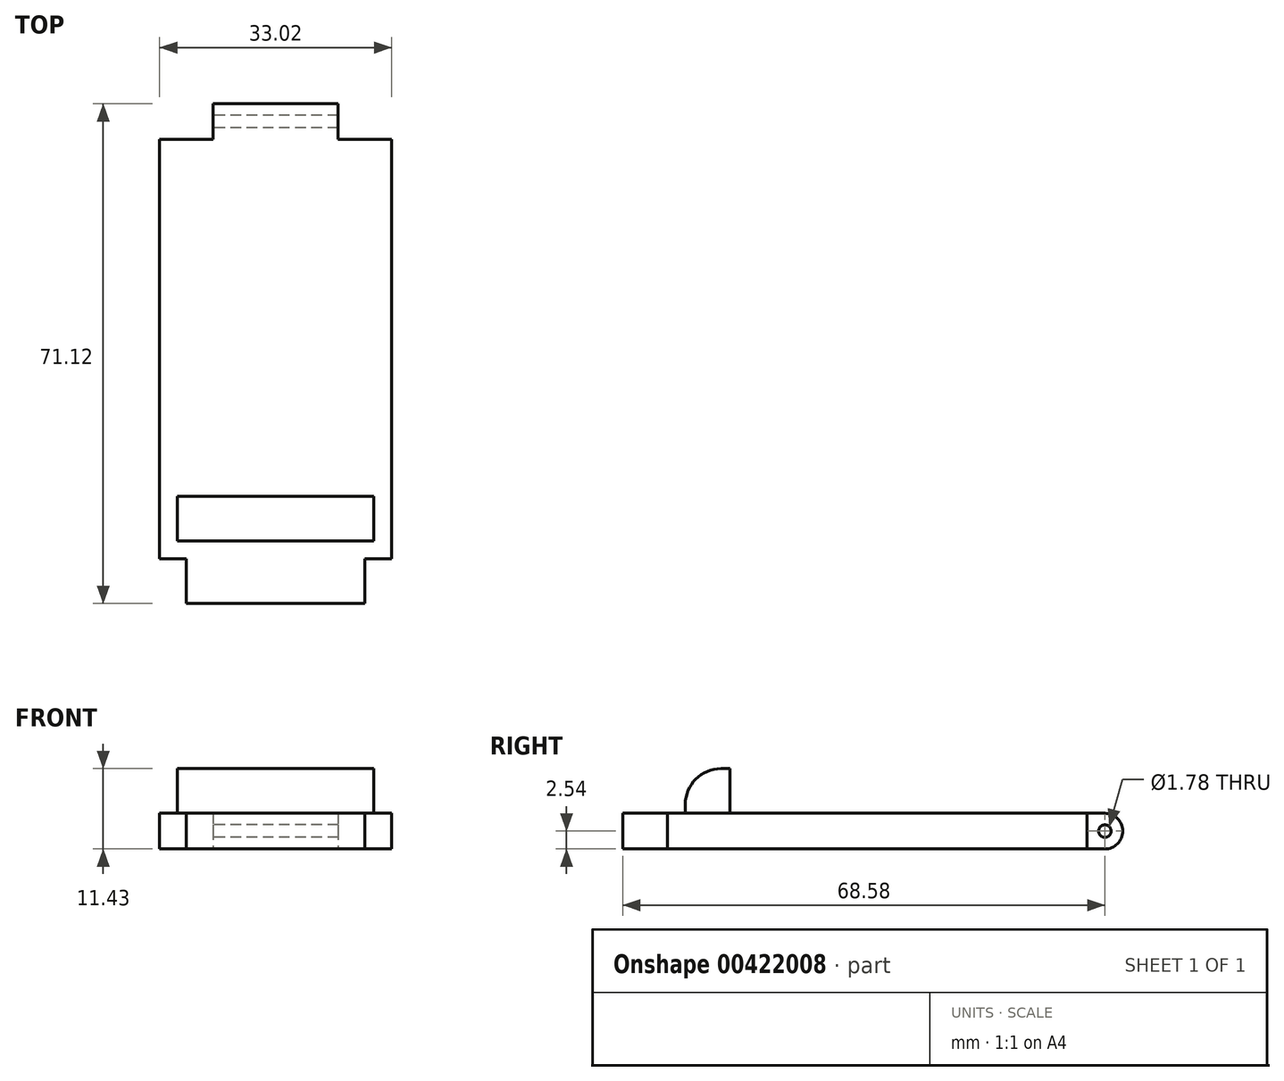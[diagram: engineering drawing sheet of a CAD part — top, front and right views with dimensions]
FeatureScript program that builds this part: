
annotation { "Feature Type Name" : "Feature", "Feature Type Description" : "" }
export const myFeature = defineFeature(function(context is Context, id is Id, definition is map)
    precondition{}
    {
        {
            var Q0;
            Q0=qCreatedBy(makeId("Top.planeOp"),FACE);
            var sketch = newSketch(context, id + "F0", { "sketchPlane" : qUnion([Q0])});
            skLineSegment(sketch, "E0.bottom", {"start": v(0, 0) * mm, "end": v(33.02, 0) * mm});
            skLineSegment(sketch, "E0.top", {"start": v(0, 59.69) * mm, "end": v(33.02, 59.69) * mm});
            skLineSegment(sketch, "E0.left", {"start": v(0, 0) * mm, "end": v(0, 59.69) * mm});
            skLineSegment(sketch, "E0.right", {"start": v(33.02, 0) * mm, "end": v(33.02, 59.69) * mm});
            skSolve(sketch);
        }
        {
            var Q0;
            Q0=makeQuery(id+"F0.imprint","IMPRINT",FACE,{"disambiguationData":[TD([[makeQuery(id+"F0.imprint","IMPRINT",EDGE,{"derivedFrom":sQuery(id+"F0.wireOp",EDGE,"E0.bottom")}),1.0]])]});
            extrude(context, id + "F1", {"entities" : qUnion([Q0]), "depth" : 5.08 * mm});
        }
        {
            var Q0;
            Q0=makeQuery(id+"F1.opExtrude","SWEPT_FACE",FACE,{"disambiguationData":[OSD([sQuery(id+"F0.wireOp",EDGE,"E0.top")])]});
            var sketch = newSketch(context, id + "F2", { "sketchPlane" : qUnion([Q0])});
            skLineSegment(sketch, "E1.bottom", {"start": v(-7.62, 5.08) * mm, "end": v(-25.4, 5.08) * mm});
            skLineSegment(sketch, "E1.top", {"start": v(-7.62, 0) * mm, "end": v(-25.4, 0) * mm});
            skLineSegment(sketch, "E1.left", {"start": v(-7.62, 5.08) * mm, "end": v(-7.62, 0) * mm});
            skLineSegment(sketch, "E1.right", {"start": v(-25.4, 5.08) * mm, "end": v(-25.4, 0) * mm});
            skSolve(sketch);
        }
        {
            var Q0;
            Q0=makeQuery(id+"F2.imprint","IMPRINT",FACE,{"disambiguationData":[TD([[makeQuery(id+"F2.imprint","IMPRINT",EDGE,{"derivedFrom":sQuery(id+"F2.wireOp",EDGE,"E1.bottom")}),1.0]])]});
            extrude(context, id + "F3", {"entities" : qUnion([Q0]), "operationType" : NewBodyOperationType.ADD, "depth" : 5.08 * mm});
        }
        {
            var Q0;
            Q0=makeQuery(id+"F3.opExtrude","SWEPT_FACE",FACE,{"disambiguationData":[OSD([sQuery(id+"F2.wireOp",EDGE,"E1.left")])]});
            var sketch = newSketch(context, id + "F4", { "sketchPlane" : qUnion([Q0])});
            skLineSegment(sketch, "E2", {"start": v(-62.23, 5.08) * mm, "end": v(-62.23, 0) * mm, "construction": true});
            skCircle(sketch, "E3", {"center": v(-62.23, 2.54) * mm, "radius": 0.89 * mm});
            skSolve(sketch);
        }
        {
            var Q0;
            Q0=makeQuery(id+"F4.imprint","IMPRINT",FACE,{"disambiguationData":[TD([[makeQuery(id+"F4.imprint","IMPRINT",EDGE,{"derivedFrom":sQuery(id+"F4.wireOp",EDGE,"E3")}),1.0]])]});
            extrude(context, id + "F5", {"entities" : qUnion([Q0]), "operationType" : NewBodyOperationType.REMOVE, "oppositeDirection" : true, "depth" : 17.78 * mm});
        }
        {
            var Q0;
            Q0=makeQuery(id+"F3.opExtrude","CAP_EDGE",EDGE,{"disambiguationData":[OSD([sQuery(id+"F2.wireOp",EDGE,"E1.top")])],"isStart":false});
            var Q1;
            Q1=makeQuery(id+"F3.opExtrude","CAP_EDGE",EDGE,{"disambiguationData":[OSD([sQuery(id+"F2.wireOp",EDGE,"E1.bottom")])],"isStart":false});
            fillet(context, id + "F6", {"entities" : qUnion([Q0, Q1]), "radius" : 2.54 * mm, "tangentPropagation" : true, "allowEdgeOverflow" : false});
        }
        {
            var Q0;
            Q0=makeQuery(id+"F3.boolean.opBoolean","MERGE",FACE,{"derivedFrom":[makeQuery(id+"F1.opExtrude","CAP_FACE",FACE,{"disambiguationData":[OSD([sQuery(id+"F0.wireOp",EDGE,"E0.bottom"),sQuery(id+"F0.wireOp",EDGE,"E0.top"),sQuery(id+"F0.wireOp",EDGE,"E0.left"),sQuery(id+"F0.wireOp",EDGE,"E0.right")])],"isStart":false}),makeQuery(id+"F3.opExtrude","SWEPT_FACE",FACE,{"disambiguationData":[OSD([sQuery(id+"F2.wireOp",EDGE,"E1.bottom")])]})]});
            var sketch = newSketch(context, id + "F7", { "sketchPlane" : qUnion([Q0])});
            skLineSegment(sketch, "E4.bottom", {"start": v(2.54, 2.54) * mm, "end": v(30.48, 2.54) * mm});
            skLineSegment(sketch, "E4.top", {"start": v(2.54, 8.89) * mm, "end": v(30.48, 8.9) * mm});
            skLineSegment(sketch, "E4.left", {"start": v(2.54, 2.54) * mm, "end": v(2.54, 8.89) * mm});
            skLineSegment(sketch, "E4.right", {"start": v(30.48, 2.54) * mm, "end": v(30.48, 8.9) * mm});
            skSolve(sketch);
        }
        {
            var Q0;
            Q0=makeQuery(id+"F7.imprint","IMPRINT",FACE,{"disambiguationData":[TD([[makeQuery(id+"F7.imprint","IMPRINT",EDGE,{"derivedFrom":sQuery(id+"F7.wireOp",EDGE,"E4.bottom")}),1.0]])]});
            extrude(context, id + "F8", {"entities" : qUnion([Q0]), "operationType" : NewBodyOperationType.ADD, "depth" : 6.35 * mm});
        }
        {
            var Q0;
            Q0=makeQuery(id+"F8.opExtrude","CAP_EDGE",EDGE,{"disambiguationData":[OSD([sQuery(id+"F7.wireOp",EDGE,"E4.bottom")])],"isStart":false});
            fillet(context, id + "F9", {"entities" : qUnion([Q0]), "radius" : 5.08 * mm, "tangentPropagation" : true, "allowEdgeOverflow" : false});
        }
        {
            var Q0;
            Q0=makeQuery(id+"F1.opExtrude","SWEPT_FACE",FACE,{"disambiguationData":[OSD([sQuery(id+"F0.wireOp",EDGE,"E0.bottom")])]});
            var sketch = newSketch(context, id + "F10", { "sketchPlane" : qUnion([Q0])});
            skLineSegment(sketch, "E5.bottom", {"start": v(3.81, 0) * mm, "end": v(29.21, 0) * mm});
            skLineSegment(sketch, "E5.top", {"start": v(3.81, 5.08) * mm, "end": v(29.21, 5.08) * mm});
            skLineSegment(sketch, "E5.left", {"start": v(3.81, 0) * mm, "end": v(3.81, 5.08) * mm});
            skLineSegment(sketch, "E5.right", {"start": v(29.21, 0) * mm, "end": v(29.21, 5.08) * mm});
            skLineSegment(sketch, "E6", {"start": v(3.81, 2.54) * mm, "end": v(0, 2.54) * mm, "construction": true});
            skLineSegment(sketch, "E7", {"start": v(29.21, 2.54) * mm, "end": v(33.02, 2.54) * mm, "construction": true});
            skSolve(sketch);
        }
        {
            var Q0;
            Q0=makeQuery(id+"F10.imprint","IMPRINT",FACE,{"disambiguationData":[TD([[makeQuery(id+"F10.imprint","IMPRINT",EDGE,{"derivedFrom":sQuery(id+"F10.wireOp",EDGE,"E5.bottom")}),1.0]])]});
            extrude(context, id + "F11", {"entities" : qUnion([Q0]), "operationType" : NewBodyOperationType.ADD, "depth" : 6.35 * mm});
        }
    });
